annotation { "Feature Type Name" : "Feature", "Feature Type Description" : "" }
export const myFeature = defineFeature(function(context is Context, id is Id, definition is map)
    precondition{}
    {
        {
            var Q0;
            Q0=qCreatedBy(makeId("Top.planeOp"),FACE);
            var sketch = newSketch(context, id + "F0", { "sketchPlane" : qUnion([Q0])});
            skLineSegment(sketch, "E0.bottom", {"start": v(-66.25, 51.1) * mm, "end": v(56.71, 51.1) * mm});
            skLineSegment(sketch, "E0.top", {"start": v(-66.25, -49.18) * mm, "end": v(56.71, -49.18) * mm});
            skLineSegment(sketch, "E0.left", {"start": v(-66.25, 51.1) * mm, "end": v(-66.25, -49.18) * mm});
            skLineSegment(sketch, "E0.right", {"start": v(56.71, 51.1) * mm, "end": v(56.71, -49.18) * mm});
            skSolve(sketch);
        }
        {
            var Q0;
            Q0=makeQuery(id+"F0.imprint","IMPRINT",FACE,{"disambiguationData":[TD([[makeQuery(id+"F0.imprint","IMPRINT",EDGE,{"derivedFrom":sQuery(id+"F0.wireOp",EDGE,"E0.bottom")}),-1.0]])]});
            extrude(context, id + "F1", {"entities" : qUnion([Q0]), "depth" : 61.81 * mm});
        }
        {
            var Q0;
            Q0=makeQuery(id+"F1.opExtrude","CAP_EDGE",EDGE,{"disambiguationData":[OSD([sQuery(id+"F0.wireOp",EDGE,"E0.top")])],"isStart":false});
            var Q1;
            Q1=makeQuery(id+"F1.opExtrude","CAP_EDGE",EDGE,{"disambiguationData":[OSD([sQuery(id+"F0.wireOp",EDGE,"E0.left")])],"isStart":false});
            var Q2;
            Q2=makeQuery(id+"F1.opExtrude","CAP_EDGE",EDGE,{"disambiguationData":[OSD([sQuery(id+"F0.wireOp",EDGE,"E0.right")])],"isStart":false});
            var Q3;
            Q3=makeQuery(id+"F1.opExtrude","CAP_EDGE",EDGE,{"disambiguationData":[OSD([sQuery(id+"F0.wireOp",EDGE,"E0.bottom")])],"isStart":false});
            fillet(context, id + "F2", {"entities" : qUnion([Q0, Q1, Q2, Q3]), "radius" : 5.08 * mm, "tangentPropagation" : true, "allowEdgeOverflow" : false});
        }
        {
            var Q0;
            Q0=makeQuery(id+"F1.opExtrude","SWEPT_FACE",FACE,{"disambiguationData":[OSD([sQuery(id+"F0.wireOp",EDGE,"E0.left")])]});
            var sketch = newSketch(context, id + "F3", { "sketchPlane" : qUnion([Q0])});
            skCircle(sketch, "E1", {"center": v(1.03, 31.7) * mm, "radius": 17.53 * mm});
            skPoint(sketch, "E1.first.point", {"position": v(-13.83, 41.02) * mm});
            skPoint(sketch, "E1.second.point", {"position": v(15.7, 22.11) * mm});
            skPoint(sketch, "E1.third.point", {"position": v(-9.89, 17.98) * mm});
            skSolve(sketch);
        }
        {
            var Q0;
            Q0=sQuery(id+"F3.wireOp",EDGE,"E1");
            extrude(context, id + "F4", {"bodyType" : ToolBodyType.SURFACE, "surfaceEntities" : qUnion([Q0]), "depth" : 3.8 * mm});
        }
        {
            var Q0;
            Q0=makeQuery(id+"F1.opExtrude","SWEPT_FACE",FACE,{"disambiguationData":[OSD([sQuery(id+"F0.wireOp",EDGE,"E0.bottom")])]});
            var sketch = newSketch(context, id + "F5", { "sketchPlane" : qUnion([Q0])});
            skLineSegment(sketch, "E2.bottom", {"start": v(-37.22, 40.56) * mm, "end": v(15, 40.56) * mm});
            skLineSegment(sketch, "E2.top", {"start": v(-37.22, 32.3) * mm, "end": v(15, 32.3) * mm});
            skLineSegment(sketch, "E2.left", {"start": v(-37.22, 40.56) * mm, "end": v(-37.22, 32.3) * mm});
            skLineSegment(sketch, "E2.right", {"start": v(15, 40.56) * mm, "end": v(15, 32.3) * mm});
            skSolve(sketch);
        }
        {
            var Q0;
            Q0=makeQuery(id+"F5.imprint","IMPRINT",FACE,{"disambiguationData":[TD([[makeQuery(id+"F5.imprint","IMPRINT",EDGE,{"derivedFrom":sQuery(id+"F5.wireOp",EDGE,"E2.bottom")}),-1.0]])]});
            extrude(context, id + "F6", {"entities" : qUnion([Q0]), "operationType" : NewBodyOperationType.ADD, "depth" : 2.74 * mm});
        }
        {
            var Q0;
            Q0=makeQuery(id+"F1.opExtrude","SWEPT_FACE",FACE,{"disambiguationData":[OSD([sQuery(id+"F0.wireOp",EDGE,"E0.bottom")])]});
            var sketch = newSketch(context, id + "F7", { "sketchPlane" : qUnion([Q0])});
            skCircle(sketch, "E3", {"center": v(36.5, 37) * mm, "radius": 6.15 * mm});
            skPoint(sketch, "E3.first.point", {"position": v(41.76, 33.83) * mm});
            skPoint(sketch, "E3.second.point", {"position": v(31.39, 40.43) * mm});
            skPoint(sketch, "E3.third.point", {"position": v(40.63, 41.56) * mm});
            skSolve(sketch);
        }
        {
            var Q0;
            Q0=makeQuery(id+"F7.imprint","IMPRINT",FACE,{"disambiguationData":[TD([[makeQuery(id+"F7.imprint","IMPRINT",EDGE,{"derivedFrom":sQuery(id+"F7.wireOp",EDGE,"E3")}),1.0]])]});
            extrude(context, id + "F8", {"entities" : qUnion([Q0]), "operationType" : NewBodyOperationType.ADD, "depth" : 3.54 * mm});
        }
        {
            var Q0;
            Q0=makeQuery(id+"F1.opExtrude","SWEPT_FACE",FACE,{"disambiguationData":[OSD([sQuery(id+"F0.wireOp",EDGE,"E0.left")])]});
            var sketch = newSketch(context, id + "F9", { "sketchPlane" : qUnion([Q0])});
            skLineSegment(sketch, "E4.bottom", {"start": v(-3.77, 34.52) * mm, "end": v(5.47, 34.52) * mm});
            skLineSegment(sketch, "E4.top", {"start": v(-3.77, 24.39) * mm, "end": v(5.47, 24.39) * mm});
            skLineSegment(sketch, "E4.left", {"start": v(-3.77, 34.52) * mm, "end": v(-3.77, 24.39) * mm});
            skLineSegment(sketch, "E4.right", {"start": v(5.47, 34.52) * mm, "end": v(5.47, 24.39) * mm});
            skSolve(sketch);
        }
        {
            var Q0;
            Q0=makeQuery(id+"F9.imprint","IMPRINT",FACE,{"disambiguationData":[TD([[makeQuery(id+"F9.imprint","IMPRINT",EDGE,{"derivedFrom":sQuery(id+"F9.wireOp",EDGE,"E4.bottom")}),-1.0]])]});
            extrude(context, id + "F10", {"entities" : qUnion([Q0]), "operationType" : NewBodyOperationType.ADD, "depth" : 41.93 * mm});
        }
        {
            var Q0;
            Q0=makeQuery(id+"F10.opExtrude","CAP_FACE",FACE,{"disambiguationData":[OSD([sQuery(id+"F9.wireOp",EDGE,"E4.bottom"),sQuery(id+"F9.wireOp",EDGE,"E4.top"),sQuery(id+"F9.wireOp",EDGE,"E4.left"),sQuery(id+"F9.wireOp",EDGE,"E4.right")])],"isStart":false});
            var sketch = newSketch(context, id + "F11", { "sketchPlane" : qUnion([Q0])});
            skLineSegment(sketch, "E5.bottom", {"start": v(-8.97, 34.95) * mm, "end": v(10.91, 34.95) * mm});
            skLineSegment(sketch, "E5.top", {"start": v(-8.97, 19.7) * mm, "end": v(10.91, 19.7) * mm});
            skLineSegment(sketch, "E5.left", {"start": v(-8.97, 34.95) * mm, "end": v(-8.97, 19.7) * mm});
            skLineSegment(sketch, "E5.right", {"start": v(10.91, 34.95) * mm, "end": v(10.91, 19.7) * mm});
            skSolve(sketch);
        }
        {
            var Q0;
            Q0=makeQuery(id+"F11.imprint","IMPRINT",FACE,{"disambiguationData":[TD([[makeQuery(id+"F11.imprint","IMPRINT",EDGE,{"derivedFrom":sQuery(id+"F11.wireOp",EDGE,"E5.bottom")}),-1.0]])]});
            extrude(context, id + "F12", {"entities" : qUnion([Q0]), "depth" : 8.05 * mm});
        }
        {
            var Q0;
            Q0=makeQuery(id+"F1.opExtrude","SWEPT_FACE",FACE,{"disambiguationData":[OSD([sQuery(id+"F0.wireOp",EDGE,"E0.right")])]});
            var sketch = newSketch(context, id + "F13", { "sketchPlane" : qUnion([Q0])});
            skLineSegment(sketch, "E6.bottom", {"start": v(-34.79, 18.83) * mm, "end": v(-20.19, 18.83) * mm});
            skLineSegment(sketch, "E6.top", {"start": v(-34.79, 9.52) * mm, "end": v(-20.19, 9.52) * mm});
            skLineSegment(sketch, "E6.left", {"start": v(-34.79, 18.83) * mm, "end": v(-34.79, 9.52) * mm});
            skLineSegment(sketch, "E6.right", {"start": v(-20.19, 18.83) * mm, "end": v(-20.19, 9.52) * mm});
            skSolve(sketch);
        }
        {
            var Q0;
            Q0=makeQuery(id+"F13.imprint","IMPRINT",FACE,{"disambiguationData":[TD([[makeQuery(id+"F13.imprint","IMPRINT",EDGE,{"derivedFrom":sQuery(id+"F13.wireOp",EDGE,"E6.bottom")}),-1.0]])]});
            extrude(context, id + "F14", {"entities" : qUnion([Q0]), "operationType" : NewBodyOperationType.ADD, "depth" : 4.16 * mm});
        }
        {
            var Q0;
            Q0=makeQuery(id+"F14.opExtrude","CAP_FACE",FACE,{"disambiguationData":[OSD([sQuery(id+"F13.wireOp",EDGE,"E6.bottom"),sQuery(id+"F13.wireOp",EDGE,"E6.top"),sQuery(id+"F13.wireOp",EDGE,"E6.left"),sQuery(id+"F13.wireOp",EDGE,"E6.right")])],"isStart":false});
            var sketch = newSketch(context, id + "F15", { "sketchPlane" : qUnion([Q0])});
            skLineSegment(sketch, "E7.bottom", {"start": v(-32.25, 16.71) * mm, "end": v(-30.77, 16.71) * mm});
            skLineSegment(sketch, "E7.top", {"start": v(-32.25, 11.64) * mm, "end": v(-30.77, 11.64) * mm});
            skLineSegment(sketch, "E7.left", {"start": v(-32.25, 16.71) * mm, "end": v(-32.25, 11.64) * mm});
            skLineSegment(sketch, "E7.right", {"start": v(-30.77, 16.71) * mm, "end": v(-30.77, 11.64) * mm});
            skLineSegment(sketch, "E8.bottom", {"start": v(-25.05, 16.71) * mm, "end": v(-23.36, 16.71) * mm});
            skLineSegment(sketch, "E8.top", {"start": v(-25.05, 11.64) * mm, "end": v(-23.36, 11.64) * mm});
            skLineSegment(sketch, "E8.left", {"start": v(-25.05, 16.71) * mm, "end": v(-25.05, 11.64) * mm});
            skLineSegment(sketch, "E8.right", {"start": v(-23.36, 16.71) * mm, "end": v(-23.36, 11.64) * mm});
            skSolve(sketch);
        }
        {
            var Q0;
            Q0=makeQuery(id+"F15.imprint","IMPRINT",FACE,{"disambiguationData":[TD([[makeQuery(id+"F15.imprint","IMPRINT",EDGE,{"derivedFrom":sQuery(id+"F15.wireOp",EDGE,"E7.bottom")}),-1.0]])]});
            var Q1;
            Q1=makeQuery(id+"F15.imprint","IMPRINT",FACE,{"disambiguationData":[TD([[makeQuery(id+"F15.imprint","IMPRINT",EDGE,{"derivedFrom":sQuery(id+"F15.wireOp",EDGE,"E8.bottom")}),-1.0]])]});
            extrude(context, id + "F16", {"entities" : qUnion([Q0, Q1]), "operationType" : NewBodyOperationType.REMOVE, "oppositeDirection" : true, "depth" : 25.4 * mm});
        }
        {
            var Q0;
            Q0=makeQuery(id+"F1.opExtrude","CAP_FACE",FACE,{"disambiguationData":[OSD([sQuery(id+"F0.wireOp",EDGE,"E0.bottom"),sQuery(id+"F0.wireOp",EDGE,"E0.top"),sQuery(id+"F0.wireOp",EDGE,"E0.left"),sQuery(id+"F0.wireOp",EDGE,"E0.right")])],"isStart":true});
            var sketch = newSketch(context, id + "F17", { "sketchPlane" : qUnion([Q0])});
            skCircle(sketch, "E9.cCircle", {"center": v(51.17, -45.74) * mm, "radius": 4.06 * mm, "construction": true});
            skLineSegment(sketch, "E9.0", {"start": v(48.63, -42.57) * mm, "end": v(53.4, -42.35) * mm});
            skLineSegment(sketch, "E9.1", {"start": v(53.4, -42.35) * mm, "end": v(55.1, -46.82) * mm});
            skLineSegment(sketch, "E9.2", {"start": v(55.1, -46.82) * mm, "end": v(51.36, -49.8) * mm});
            skLineSegment(sketch, "E9.3", {"start": v(51.36, -49.8) * mm, "end": v(47.37, -47.18) * mm});
            skLineSegment(sketch, "E9.4", {"start": v(47.37, -47.18) * mm, "end": v(48.63, -42.57) * mm});
            skCircle(sketch, "E10.cCircle", {"center": v(-59.69, -46.8) * mm, "radius": 3.78 * mm, "construction": true});
            skLineSegment(sketch, "E10.0", {"start": v(-56.3, -45.1) * mm, "end": v(-56.53, -48.89) * mm});
            skLineSegment(sketch, "E10.1", {"start": v(-56.53, -48.89) * mm, "end": v(-59.91, -50.58) * mm});
            skLineSegment(sketch, "E10.2", {"start": v(-59.91, -50.58) * mm, "end": v(-63.07, -48.5) * mm});
            skLineSegment(sketch, "E10.3", {"start": v(-63.07, -48.5) * mm, "end": v(-62.85, -44.72) * mm});
            skLineSegment(sketch, "E10.4", {"start": v(-62.85, -44.72) * mm, "end": v(-59.46, -43.02) * mm});
            skLineSegment(sketch, "E10.5", {"start": v(-59.46, -43.02) * mm, "end": v(-56.3, -45.1) * mm});
            skCircle(sketch, "E11.cCircle", {"center": v(51.17, 43.11) * mm, "radius": 4.17 * mm, "construction": true});
            skLineSegment(sketch, "E11.0", {"start": v(49.06, 46.71) * mm, "end": v(53.23, 46.74) * mm});
            skLineSegment(sketch, "E11.1", {"start": v(53.23, 46.74) * mm, "end": v(55.34, 43.15) * mm});
            skLineSegment(sketch, "E11.2", {"start": v(55.34, 43.15) * mm, "end": v(53.29, 39.52) * mm});
            skLineSegment(sketch, "E11.3", {"start": v(53.29, 39.52) * mm, "end": v(49.11, 39.48) * mm});
            skLineSegment(sketch, "E11.4", {"start": v(49.11, 39.48) * mm, "end": v(47, 43.08) * mm});
            skLineSegment(sketch, "E11.5", {"start": v(47, 43.08) * mm, "end": v(49.06, 46.71) * mm});
            skCircle(sketch, "E12.cCircle", {"center": v(-59.05, 43.33) * mm, "radius": 4.66 * mm, "construction": true});
            skLineSegment(sketch, "E12.0", {"start": v(-54.4, 43.54) * mm, "end": v(-56.54, 39.4) * mm});
            skLineSegment(sketch, "E12.1", {"start": v(-56.54, 39.4) * mm, "end": v(-61.2, 39.19) * mm});
            skLineSegment(sketch, "E12.2", {"start": v(-61.2, 39.19) * mm, "end": v(-63.7, 43.11) * mm});
            skLineSegment(sketch, "E12.3", {"start": v(-63.7, 43.11) * mm, "end": v(-61.56, 47.25) * mm});
            skLineSegment(sketch, "E12.4", {"start": v(-61.56, 47.25) * mm, "end": v(-56.9, 47.46) * mm});
            skLineSegment(sketch, "E12.5", {"start": v(-56.9, 47.46) * mm, "end": v(-54.4, 43.54) * mm});
            skSolve(sketch);
        }
        {
            var Q0;
            Q0=makeQuery(id+"F17.imprint","IMPRINT",FACE,{"disambiguationData":[TD([[makeQuery(id+"F17.imprint","IMPRINT",EDGE,{"derivedFrom":sQuery(id+"F17.wireOp",EDGE,"E9.0")}),-1.0]])]});
            var Q1;
            Q1=makeQuery(id+"F17.imprint","IMPRINT",FACE,{"disambiguationData":[TD([[makeQuery(id+"F17.imprint","IMPRINT",EDGE,{"derivedFrom":sQuery(id+"F17.wireOp",EDGE,"E11.0")}),-1.0]])]});
            var Q2;
            Q2=makeQuery(id+"F17.imprint","IMPRINT",FACE,{"disambiguationData":[TD([[makeQuery(id+"F17.imprint","IMPRINT",EDGE,{"derivedFrom":sQuery(id+"F17.wireOp",EDGE,"E12.0")}),-1.0]])]});
            var Q3;
            Q3=makeQuery(id+"F17.imprint","IMPRINT",FACE,{"disambiguationData":[TD([[makeQuery(id+"F17.imprint","IMPRINT",EDGE,{"derivedFrom":sQuery(id+"F17.wireOp",EDGE,"E10.0")}),-1.0]])]});
            extrude(context, id + "F18", {"entities" : qUnion([Q0, Q1, Q2, Q3]), "operationType" : NewBodyOperationType.ADD, "depth" : 1.76 * mm});
        }
        {
            var Q0;
            Q0=makeQuery(id+"F1.opExtrude","SWEPT_FACE",FACE,{"disambiguationData":[OSD([sQuery(id+"F0.wireOp",EDGE,"E0.top")])]});
            var sketch = newSketch(context, id + "F19", { "sketchPlane" : qUnion([Q0])});
            skSolve(sketch);
        }
        {
            var Q0;
            {var subQ0=sQuery(id+"F0.wireOp",EDGE,"E0.top");Q0=makeQuery(id+"F19.imprint","IMPRINT",FACE,{"disambiguationData":[TD([[makeQuery(id+"F19.imprint","IMPRINT",EDGE,{"derivedFrom":makeQuery(id+"F1.opExtrude","CAP_EDGE",EDGE,{"disambiguationData":[OSD([subQ0])],"isStart":true})}),1.0]])]});}
            var sketch = newSketch(context, id + "F20", { "sketchPlane" : qUnion([Q0])});
            skText(sketch, "E13", { "text": "Cut-Boy 3000", "fontName": "OpenSans-Italic.ttf"});
            const initialGuessF20  = {"E13": [-0.06042, 0.04208, 1, 0, 0.01211]};
            skSetInitialGuess(sketch, initialGuessF20);
            skSolve(sketch);
        }
        {
            var Q0;
            Q0 = qSketchRegion(id + "F20", true);
            extrude(context, id + "F21", {"entities" : qUnion([Q0]), "operationType" : NewBodyOperationType.ADD, "depth" : 1.95 * mm});
        }
        {
            var Q0;
            {var subQ0=sQuery(id+"F0.wireOp",EDGE,"E0.top");Q0=makeQuery(id+"F19.imprint","IMPRINT",FACE,{"disambiguationData":[TD([[makeQuery(id+"F19.imprint","IMPRINT",EDGE,{"derivedFrom":makeQuery(id+"F1.opExtrude","CAP_EDGE",EDGE,{"disambiguationData":[OSD([subQ0])],"isStart":true})}),1.0]])]});}
            var sketch = newSketch(context, id + "F22", { "sketchPlane" : qUnion([Q0])});
            skText(sketch, "E14", { "text": "Gold Edition", "fontName": "OpenSans-Italic.ttf"});
            const initialGuessF22  = {"E14": [-0.05862, 0.0171, 1, 0, 0.01427]};
            skSetInitialGuess(sketch, initialGuessF22);
            skSolve(sketch);
        }
        {
            var Q0;
            Q0 = qSketchRegion(id + "F22", true);
            extrude(context, id + "F23", {"entities" : qUnion([Q0]), "operationType" : NewBodyOperationType.ADD, "depth" : 1.52 * mm});
        }
    });